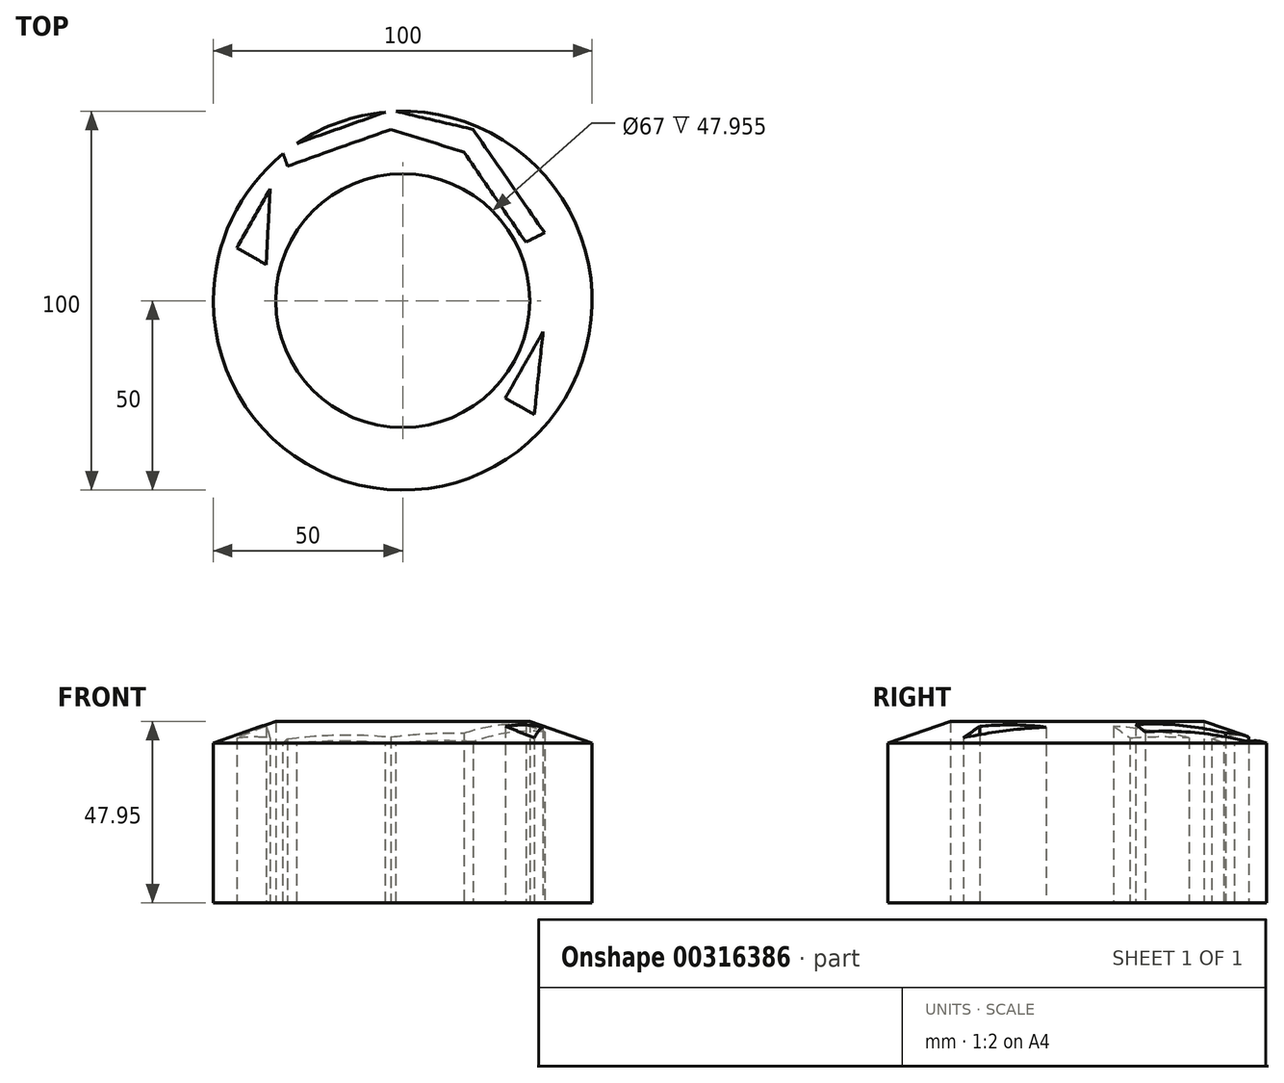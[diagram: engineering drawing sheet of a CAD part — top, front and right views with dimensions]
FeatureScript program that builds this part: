
annotation { "Feature Type Name" : "Feature", "Feature Type Description" : "" }
export const myFeature = defineFeature(function(context is Context, id is Id, definition is map)
    precondition{}
    {
        {
            var Q0;
            Q0=qCreatedBy(makeId("Front.planeOp"),FACE);
            var sketch = newSketch(context, id + "F0", { "sketchPlane" : qUnion([Q0])});
            skLineSegment(sketch, "E0", {"start": v(0, 0) * mm, "end": v(0, 59.73) * mm});
            skLineSegment(sketch, "E1", {"start": v(0, 59.73) * mm, "end": v(50, 42.15) * mm});
            skLineSegment(sketch, "E2", {"start": v(50, 42.15) * mm, "end": v(50, 0) * mm});
            skLineSegment(sketch, "E3", {"start": v(50, 0) * mm, "end": v(0, 0) * mm});
            skLineSegment(sketch, "E4", {"start": v(0, 74.34) * mm, "end": v(0, -13.6) * mm, "construction": true});
            skSolve(sketch);
        }
        {
            var Q0;
            Q0=makeQuery(id+"F0.imprint","IMPRINT",FACE,{"disambiguationData":[TD([[makeQuery(id+"F0.imprint","IMPRINT",EDGE,{"derivedFrom":sQuery(id+"F0.wireOp",EDGE,"E0")}),-1.0]])]});
            var Q1;
            Q1=sQuery(id+"F0.wireOp",EDGE,"E4");
            revolve(context, id + "F1", {"entities" : qUnion([Q0]), "axis" : qUnion([Q1]), "revolveType" : RevolveType.FULL});
        }
        {
            var Q0;
            Q0=qCreatedBy(makeId("Top.planeOp"),FACE);
            var sketch = newSketch(context, id + "F2", { "sketchPlane" : qUnion([Q0])});
            skCircle(sketch, "E5", {"center": v(0, 0) * mm, "radius": 33.5 * mm});
            skSolve(sketch);
        }
        {
            var Q0;
            Q0=makeQuery(id+"F2.imprint","IMPRINT",FACE,{"disambiguationData":[TD([[makeQuery(id+"F2.imprint","IMPRINT",EDGE,{"derivedFrom":sQuery(id+"F2.wireOp",EDGE,"E5")}),1.0]])]});
            extrude(context, id + "F3", {"entities" : qUnion([Q0]), "operationType" : NewBodyOperationType.REMOVE, "depth" : 60.3 * mm});
        }
        {
            var Q0;
            Q0=qCreatedBy(makeId("Top.planeOp"),FACE);
            var sketch = newSketch(context, id + "F4", { "sketchPlane" : qUnion([Q0])});
            skLineSegment(sketch, "E6", {"start": v(-35, 29.5) * mm, "end": v(-43.83, 13.95) * mm});
            skLineSegment(sketch, "E7", {"start": v(-43.83, 13.95) * mm, "end": v(-36.05, 9.53) * mm});
            skLineSegment(sketch, "E8", {"start": v(-36.05, 9.53) * mm, "end": v(-35, 29.5) * mm});
            skLineSegment(sketch, "E9", {"start": v(37.03, -8.17) * mm, "end": v(27.07, -25.72) * mm});
            skLineSegment(sketch, "E10", {"start": v(27.07, -25.72) * mm, "end": v(34.72, -30.07) * mm});
            skLineSegment(sketch, "E11", {"start": v(34.72, -30.07) * mm, "end": v(37.03, -8.17) * mm});
            skSolve(sketch);
        }
        {
            var Q0;
            Q0=makeQuery(id+"F4.imprint","IMPRINT",FACE,{"disambiguationData":[TD([[makeQuery(id+"F4.imprint","IMPRINT",EDGE,{"derivedFrom":sQuery(id+"F4.wireOp",EDGE,"E9")}),1.0]])]});
            var Q1;
            Q1=makeQuery(id+"F4.imprint","IMPRINT",FACE,{"disambiguationData":[TD([[makeQuery(id+"F4.imprint","IMPRINT",EDGE,{"derivedFrom":sQuery(id+"F4.wireOp",EDGE,"E6")}),1.0]])]});
            extrude(context, id + "F5", {"entities" : qUnion([Q0, Q1]), "operationType" : NewBodyOperationType.REMOVE, "depth" : 185.2 * mm});
        }
        {
            var Q0;
            Q0=qCreatedBy(makeId("Top.planeOp"),FACE);
            var sketch = newSketch(context, id + "F6", { "sketchPlane" : qUnion([Q0])});
            skLineSegment(sketch, "E12", {"start": v(32.5, 15.42) * mm, "end": v(16.2, 39.2) * mm});
            skLineSegment(sketch, "E13", {"start": v(16.2, 39.2) * mm, "end": v(-3.15, 45.2) * mm});
            skLineSegment(sketch, "E14", {"start": v(-3.15, 45.2) * mm, "end": v(-30.41, 35.53) * mm});
            skLineSegment(sketch, "E15", {"start": v(-30.41, 35.53) * mm, "end": v(-32.02, 40.04) * mm});
            skLineSegment(sketch, "E16", {"start": v(-32.02, 40.04) * mm, "end": v(-3.15, 50.3) * mm});
            skLineSegment(sketch, "E17", {"start": v(-3.15, 50.3) * mm, "end": v(18.54, 45.2) * mm});
            skLineSegment(sketch, "E18", {"start": v(18.54, 45.2) * mm, "end": v(37.44, 17.94) * mm});
            skLineSegment(sketch, "E19", {"start": v(37.44, 17.94) * mm, "end": v(32.5, 15.42) * mm});
            skSolve(sketch);
        }
        {
            var Q0;
            Q0=makeQuery(id+"F6.imprint","IMPRINT",FACE,{"disambiguationData":[TD([[makeQuery(id+"F6.imprint","IMPRINT",EDGE,{"derivedFrom":sQuery(id+"F6.wireOp",EDGE,"E12")}),-1.0]])]});
            extrude(context, id + "F7", {"entities" : qUnion([Q0]), "operationType" : NewBodyOperationType.REMOVE, "depth" : 513.9 * mm});
        }
    });
